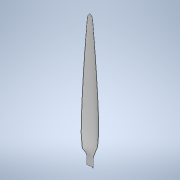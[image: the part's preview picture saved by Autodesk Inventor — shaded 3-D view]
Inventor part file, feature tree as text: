
AUTODESK INVENTOR PART (.ipt)
format: ipt  version: 2022 (Build 260153000, 153)  size: 985,088 bytes
history: native  units: mm
features: sketch x3, sweep x1
ambient origin geometry x8: Origin, YZ Plane, XZ Plane, XY Plane, X Axis, Y Axis, Z Axis, Center Point
bodies: Solid1 (feature_tree)
feature tree (4):
  sweep  "Sweep1"
  sketch  "Sketch1"  dims[d0=330.0mm d1=90.0deg]
  sketch  "Sketch2"  dims[d6=0.0mm d7=0.0mm]
  sketch  "3D Sketch1"
